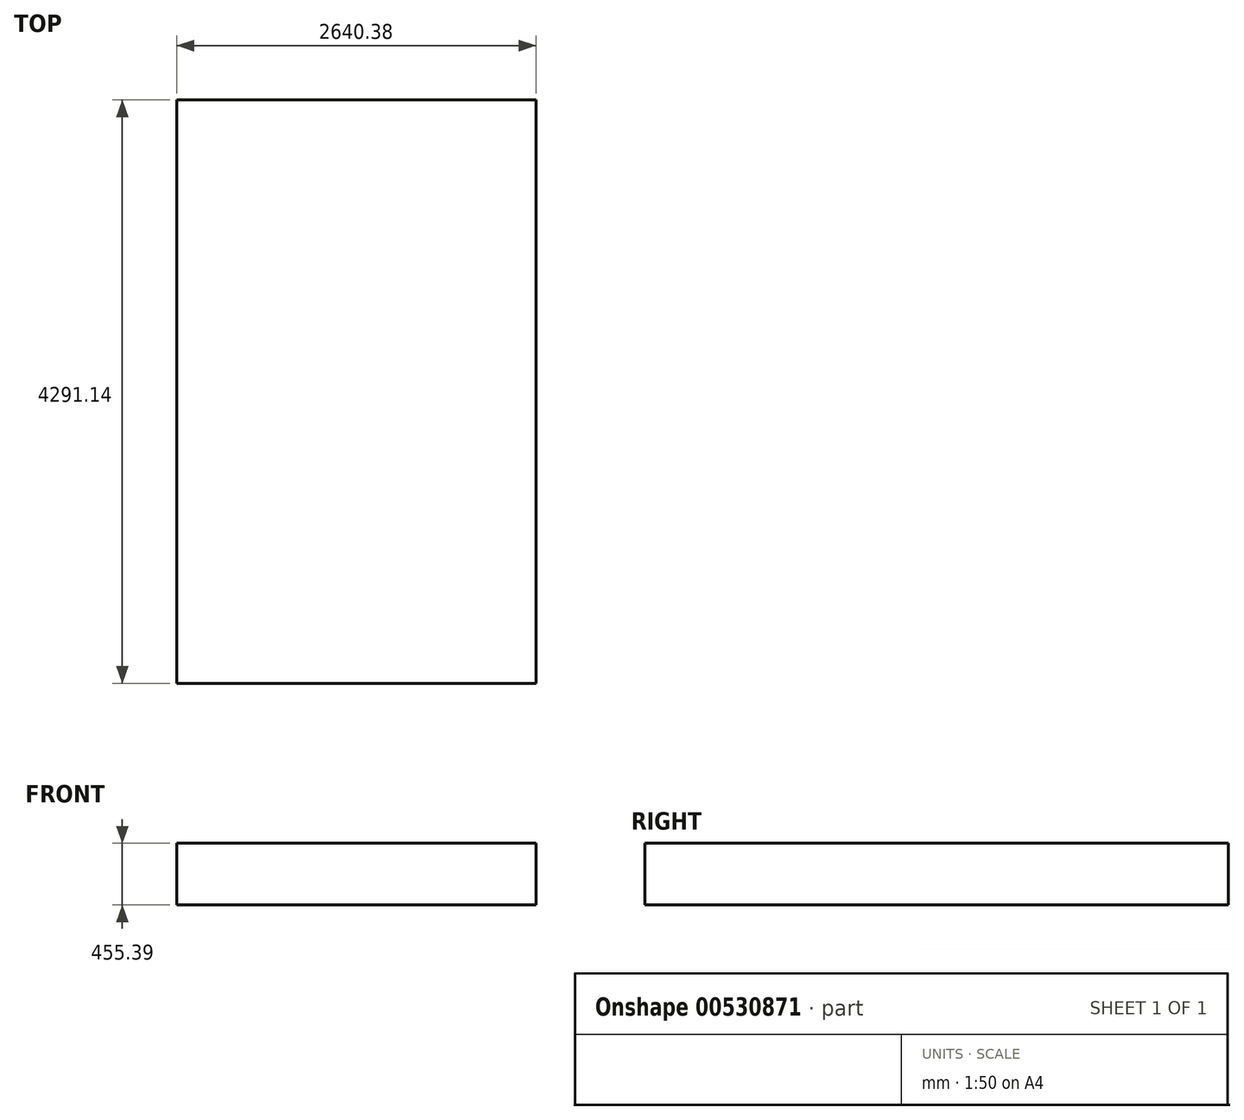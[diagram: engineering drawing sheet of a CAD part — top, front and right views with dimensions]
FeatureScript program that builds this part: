
annotation { "Feature Type Name" : "Feature", "Feature Type Description" : "" }
export const myFeature = defineFeature(function(context is Context, id is Id, definition is map)
    precondition{}
    {
        {
            var Q0;
            Q0=qCreatedBy(makeId("Top.planeOp"),FACE);
            var sketch = newSketch(context, id + "F0", { "sketchPlane" : qUnion([Q0])});
            skLineSegment(sketch, "E0.bottom", {"start": v(1320.19, -2145.57) * mm, "end": v(-1320.19, -2145.57) * mm});
            skLineSegment(sketch, "E0.top", {"start": v(1320.19, 2145.57) * mm, "end": v(-1320.19, 2145.57) * mm});
            skLineSegment(sketch, "E0.left", {"start": v(1320.19, -2145.57) * mm, "end": v(1320.19, 2145.57) * mm});
            skLineSegment(sketch, "E0.right", {"start": v(-1320.19, -2145.57) * mm, "end": v(-1320.19, 2145.57) * mm});
            skPoint(sketch, "E0.middle", {"position": v(0, 0) * mm});
            skSolve(sketch);
        }
        {
            var Q0;
            Q0=makeQuery(id+"F0.imprint","IMPRINT",FACE,{"disambiguationData":[TD([[makeQuery(id+"F0.imprint","IMPRINT",EDGE,{"derivedFrom":sQuery(id+"F0.wireOp",EDGE,"E0.bottom")}),-1.0]])]});
            extrude(context, id + "F1", {"entities" : qUnion([Q0]), "depth" : 455.4 * mm, "offsetDistance" : 25.4 * mm});
        }
    });
